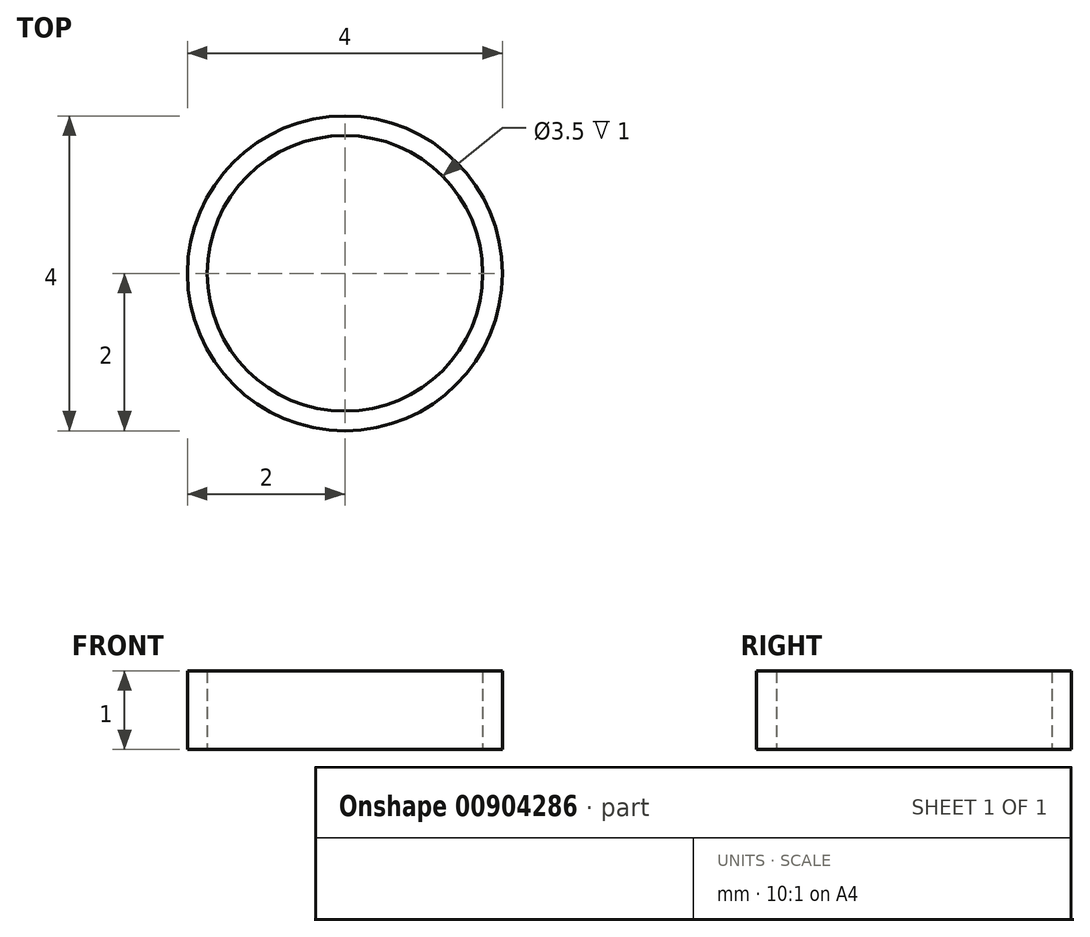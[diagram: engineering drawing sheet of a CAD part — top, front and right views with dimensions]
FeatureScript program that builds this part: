
annotation { "Feature Type Name" : "Feature", "Feature Type Description" : "" }
export const myFeature = defineFeature(function(context is Context, id is Id, definition is map)
    precondition{}
    {
        {
            var Q0;
            Q0=qCreatedBy(makeId("Front.planeOp"),FACE);
            var sketch = newSketch(context, id + "F0", { "sketchPlane" : qUnion([Q0])});
            skLineSegment(sketch, "E0.bottom", {"start": v(0, 0) * mm, "end": v(-1.75, 0) * mm});
            skLineSegment(sketch, "E0.top", {"start": v(0, 1) * mm, "end": v(-1.75, 1) * mm});
            skLineSegment(sketch, "E0.left", {"start": v(0, 0) * mm, "end": v(0, 1) * mm});
            skLineSegment(sketch, "E0.right", {"start": v(-1.75, 0) * mm, "end": v(-1.75, 1) * mm});
            skLineSegment(sketch, "E1.bottom", {"start": v(0, 0) * mm, "end": v(-2, 0) * mm});
            skLineSegment(sketch, "E1.top", {"start": v(0, 1) * mm, "end": v(-2, 1) * mm});
            skLineSegment(sketch, "E1.right", {"start": v(-2, 0) * mm, "end": v(-2, 1) * mm});
            skSolve(sketch);
        }
        {
            var Q0;
            {var subQ0=sQuery(id+"F0.wireOp",EDGE,"E0.right");Q0=makeQuery(id+"F0.imprint","IMPRINT",FACE,{"disambiguationData":[TD([[makeQuery(id+"F0.imprint","IMPRINT",EDGE,{"derivedFrom":subQ0}),1.0]])]});}
            var Q1;
            Q1=sQuery(id+"F0.wireOp",EDGE,"E0.left");
            revolve(context, id + "F1", {"surfaceOperationType" : NewSurfaceOperationType.NEW, "entities" : qUnion([Q0]), "axis" : qUnion([Q1]), "revolveType" : RevolveType.FULL});
        }
    });
